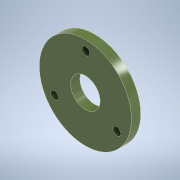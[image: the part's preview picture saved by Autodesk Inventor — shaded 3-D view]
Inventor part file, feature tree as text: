
AUTODESK INVENTOR PART (.ipt)
format: ipt  version: 2021 (Build 250183000, 183)  size: 117,248 bytes
history: native  units: mm
features: extrude x2, sketch x2, other x1, pattern_circular x1
ambient origin geometry x8: Origin, YZ Plane, XZ Plane, XY Plane, X Axis, Y Axis, Z Axis, Center Point
bodies: Body1 (feature_tree)
feature tree (6):
  other  "Sólido1"
  extrude  "Extrusão1"  Depth=16.0mm
  extrude  "Extrusão2"  Depth=5.0mm
  pattern_circular  "Padrão circular1"  [2 undecoded]
  sketch  "Esboço1"  dims[d0=50.0mm d1=16.0mm]
  sketch  "Esboço2"  dims[d2=5.0mm d3=0.0mm d4=28.0mm d5=4.5mm d6=0.0mm d7=0.0mm d8=30.0mm d9=360.0deg]
note: 2 required parameter values undecoded (feature->parameter linkage not recoverable at this tier; creation-order binding heuristic only, values carry confidence <= 0.55)
